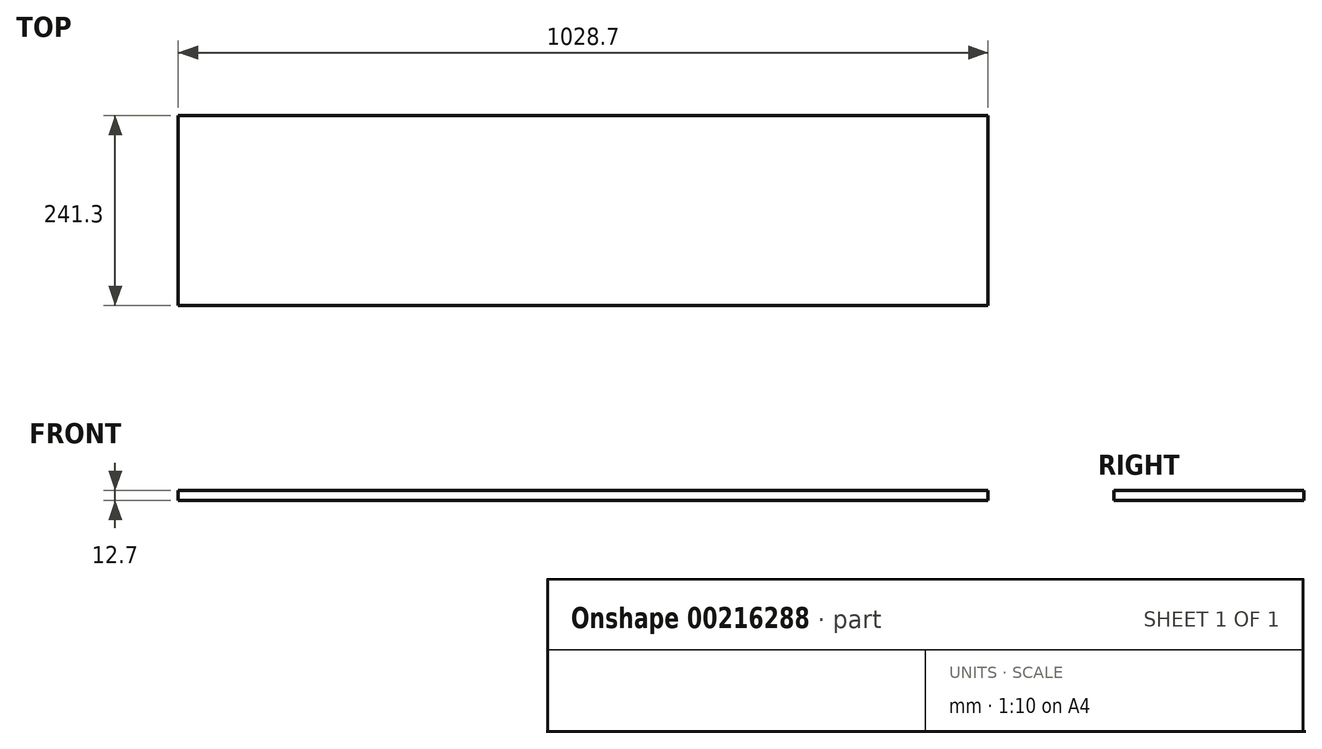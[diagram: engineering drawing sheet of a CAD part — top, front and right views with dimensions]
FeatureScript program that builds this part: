
annotation { "Feature Type Name" : "Feature", "Feature Type Description" : "" }
export const myFeature = defineFeature(function(context is Context, id is Id, definition is map)
    precondition{}
    {
        {
            var Q0;
            Q0=qCreatedBy(makeId("Top.planeOp"),FACE);
            var sketch = newSketch(context, id + "F0", { "sketchPlane" : qUnion([Q0])});
            skArc(sketch, "E0", {"start": v(-5251.06, 895.22) * mm, "mid": v(-5538.43, 895.22) * mm, "end": v(-5538.43, 607.85) * mm});
            skArc(sketch, "E1", {"start": v(-5430.67, 500.08) * mm, "mid": v(-5143.3, 500.08) * mm, "end": v(-5143.3, 787.45) * mm});
            skLineSegment(sketch, "E2", {"start": v(-5251.06, 895.22) * mm, "end": v(-5143.3, 787.45) * mm});
            skLineSegment(sketch, "E3", {"start": v(-5538.43, 607.85) * mm, "end": v(-5430.67, 500.08) * mm});
            skLineSegment(sketch, "E4", {"start": v(-8374.52, 1221.43) * mm, "end": v(-7345.82, 1221.43) * mm});
            skLineSegment(sketch, "E5", {"start": v(-7409.32, -1978.97) * mm, "end": v(-4869.32, -1978.97) * mm});
            skLineSegment(sketch, "E6", {"start": v(-7409.32, -1449.55) * mm, "end": v(-7409.32, -1978.97) * mm});
            skLineSegment(sketch, "E7", {"start": v(-7345.82, 980.13) * mm, "end": v(-8374.52, 980.13) * mm});
            skLineSegment(sketch, "E8", {"start": v(-8374.52, 992.83) * mm, "end": v(-8374.52, 1221.43) * mm});
            skLineSegment(sketch, "E9", {"start": v(-7345.82, 980.13) * mm, "end": v(-6723.52, 980.13) * mm});
            skLineSegment(sketch, "E10", {"start": v(-7345.82, 980.13) * mm, "end": v(-7345.82, 1221.43) * mm});
            skLineSegment(sketch, "E11", {"start": v(-5467.14, -705.4) * mm, "end": v(-5897.87, -225.9) * mm});
            skLineSegment(sketch, "E12", {"start": v(-4869.32, -1978.97) * mm, "end": v(-4869.32, 1221.43) * mm});
            skLineSegment(sketch, "E13", {"start": v(-7345.82, 1221.43) * mm, "end": v(-4869.32, 1221.43) * mm});
            skLineSegment(sketch, "E14", {"start": v(-7460.12, 281.63) * mm, "end": v(-6960.57, 281.63) * mm});
            skLineSegment(sketch, "E15", {"start": v(-5587.74, -1477.13) * mm, "end": v(-5472.75, -1362.15) * mm});
            skLineSegment(sketch, "E16", {"start": v(-5928.07, -1521.77) * mm, "end": v(-5695.5, -1521.77) * mm});
            skArc(sketch, "E17", {"start": v(-5695.5, -1521.77) * mm, "mid": v(-5637.18, -1510.17) * mm, "end": v(-5587.74, -1477.13) * mm});
            skLineSegment(sketch, "E18", {"start": v(-5428.12, -807.23) * mm, "end": v(-5428.12, -1254.38) * mm});
            skArc(sketch, "E19", {"start": v(-5428.12, -807.23) * mm, "mid": v(-5438.2, -752.7) * mm, "end": v(-5467.14, -705.4) * mm});
            skArc(sketch, "E20", {"start": v(-5472.75, -1362.15) * mm, "mid": v(-5439.72, -1312.7) * mm, "end": v(-5428.12, -1254.38) * mm});
            skLineSegment(sketch, "E21", {"start": v(-6822.36, 193.46) * mm, "end": v(-6066.27, -1433.6) * mm});
            skArc(sketch, "E22", {"start": v(-6066.27, -1433.6) * mm, "mid": v(-6010.04, -1497.85) * mm, "end": v(-5928.07, -1521.77) * mm});
            skArc(sketch, "E23", {"start": v(-6822.36, 193.46) * mm, "mid": v(-6878.6, 257.71) * mm, "end": v(-6960.57, 281.63) * mm});
            skLineSegment(sketch, "E24", {"start": v(-6113.92, 209.42) * mm, "end": v(-6113.92, 370.53) * mm});
            skLineSegment(sketch, "E25", {"start": v(-6099.72, 145.2) * mm, "end": v(-5997.2, -75.42) * mm});
            skArc(sketch, "E26", {"start": v(-6113.92, 209.42) * mm, "mid": v(-6110.33, 176.53) * mm, "end": v(-6099.72, 145.2) * mm});
            skArc(sketch, "E27", {"start": v(-5997.2, -75.42) * mm, "mid": v(-5953.13, -154.35) * mm, "end": v(-5897.87, -225.9) * mm});
            skArc(sketch, "E28", {"start": v(-6113.92, 370.53) * mm, "mid": v(-6292.46, 801.58) * mm, "end": v(-6723.52, 980.13) * mm});
            skLineSegment(sketch, "E29", {"start": v(-7612.52, -242.32) * mm, "end": v(-7612.52, 129.23) * mm});
            skArc(sketch, "E30", {"start": v(-7460.12, 281.63) * mm, "mid": v(-7567.88, 237) * mm, "end": v(-7612.52, 129.23) * mm});
            skLineSegment(sketch, "E31", {"start": v(-7411.52, -1423.72) * mm, "end": v(-7610.3, -268.16) * mm});
            skArc(sketch, "E32", {"start": v(-7409.32, -1449.55) * mm, "mid": v(-7409.87, -1436.59) * mm, "end": v(-7411.52, -1423.72) * mm});
            skArc(sketch, "E33", {"start": v(-7612.52, -242.32) * mm, "mid": v(-7611.96, -255.29) * mm, "end": v(-7610.3, -268.16) * mm});
            skLineSegment(sketch, "E34", {"start": v(-8374.52, 980.13) * mm, "end": v(-8374.52, 1221.43) * mm});
            skSolve(sketch);
        }
        {
            var Q0;
            {var subQ0=sQuery(id+"F0.wireOp",EDGE,"E4");Q0=makeQuery(id+"F0.imprint","IMPRINT",FACE,{"disambiguationData":[TD([[makeQuery(id+"F0.imprint","IMPRINT",EDGE,{"derivedFrom":subQ0}),-1.0]])]});}
            extrude(context, id + "F1", {"entities" : qUnion([Q0]), "depth" : 12.7 * mm});
        }
    });
